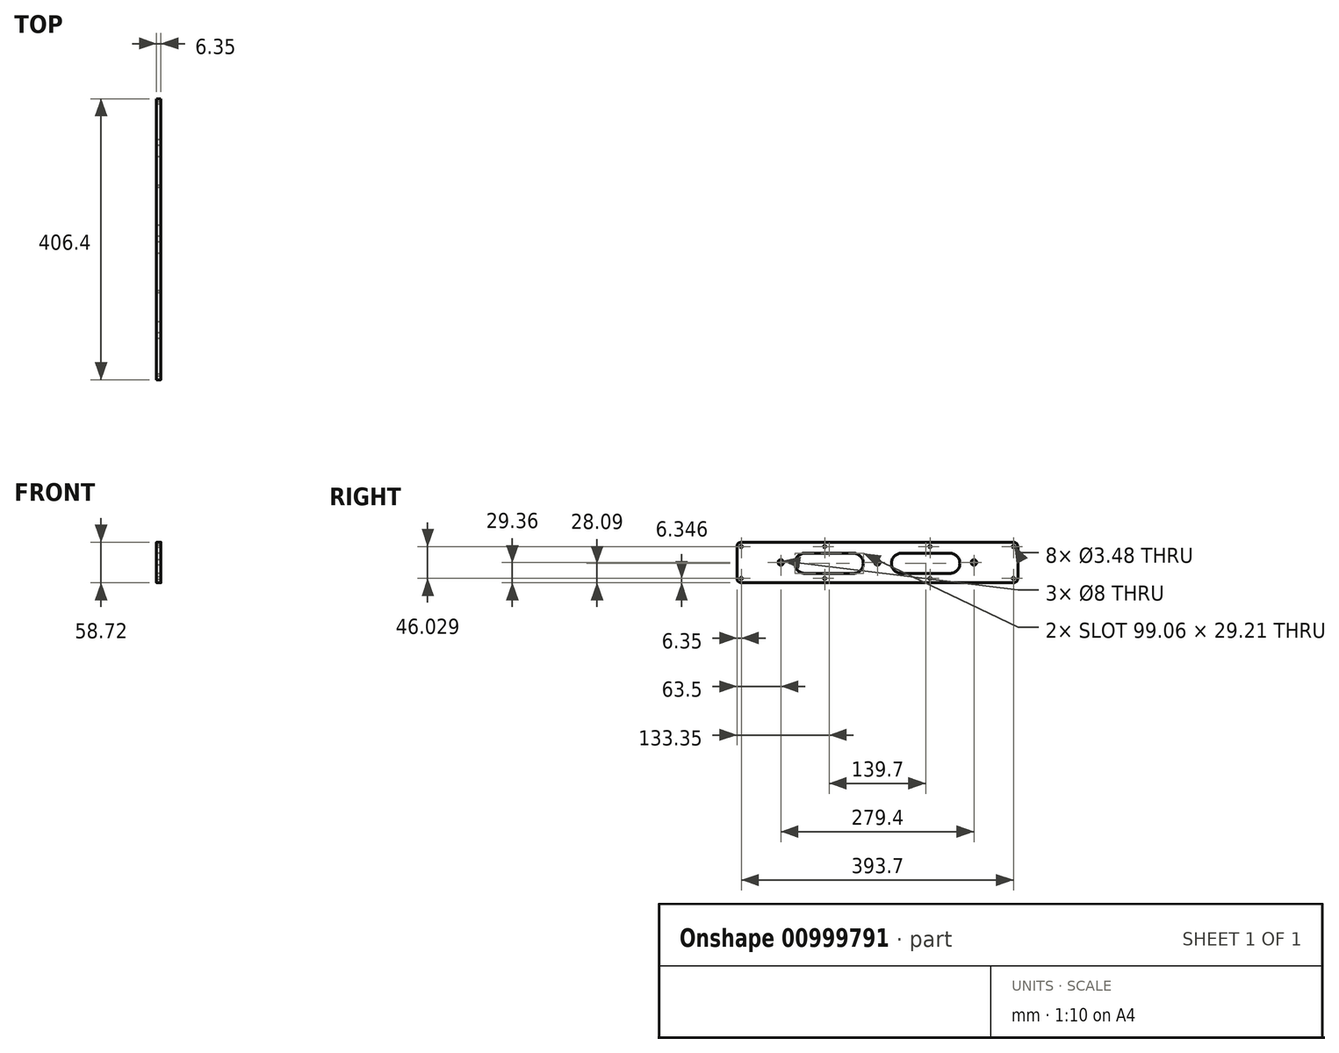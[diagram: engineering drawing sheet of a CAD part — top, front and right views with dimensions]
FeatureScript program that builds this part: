
annotation { "Feature Type Name" : "Feature", "Feature Type Description" : "" }
export const myFeature = defineFeature(function(context is Context, id is Id, definition is map)
    precondition{}
    {
        {
            var Q0;
            Q0=qCreatedBy(makeId("Right.planeOp"),FACE);
            var sketch = newSketch(context, id + "F0", { "sketchPlane" : qUnion([Q0])});
            skLineSegment(sketch, "E0.bottom", {"start": v(-196.85, -29.36) * mm, "end": v(196.85, -29.36) * mm});
            skLineSegment(sketch, "E0.top", {"start": v(-196.85, 29.36) * mm, "end": v(196.85, 29.36) * mm});
            skLineSegment(sketch, "E0.left", {"start": v(-203.2, -23.01) * mm, "end": v(-203.2, 23.01) * mm});
            skLineSegment(sketch, "E0.right", {"start": v(203.2, -23.01) * mm, "end": v(203.2, 23.01) * mm});
            skPoint(sketch, "E0.middle", {"position": v(0, 0) * mm});
            skCircle(sketch, "E1", {"center": v(0, 0) * mm, "radius": 4 * mm});
            skPoint(sketch, "E2.visualSharp", {"position": v(-203.2, 29.36) * mm});
            skArc(sketch, "E2.filletArc", {"start": v(-196.85, 29.36) * mm, "mid": v(-201.34, 27.5) * mm, "end": v(-203.2, 23.01) * mm});
            skPoint(sketch, "E3.visualSharp", {"position": v(-203.2, -29.36) * mm});
            skArc(sketch, "E3.filletArc", {"start": v(-203.2, -23.01) * mm, "mid": v(-201.34, -27.5) * mm, "end": v(-196.85, -29.36) * mm});
            skPoint(sketch, "E4.visualSharp", {"position": v(203.2, 29.36) * mm});
            skArc(sketch, "E4.filletArc", {"start": v(203.2, 23.01) * mm, "mid": v(201.34, 27.5) * mm, "end": v(196.85, 29.36) * mm});
            skPoint(sketch, "E5.visualSharp", {"position": v(203.2, -29.36) * mm});
            skArc(sketch, "E5.filletArc", {"start": v(196.85, -29.36) * mm, "mid": v(201.34, -27.5) * mm, "end": v(203.2, -23.01) * mm});
            skCircle(sketch, "E6", {"center": v(139.7, 0) * mm, "radius": 4 * mm});
            skCircle(sketch, "E7", {"center": v(-139.7, 0) * mm, "radius": 4 * mm});
            skCircle(sketch, "E8", {"center": v(196.85, 23.01) * mm, "radius": 1.74 * mm});
            skCircle(sketch, "E9", {"center": v(196.85, -23.01) * mm, "radius": 1.74 * mm});
            skCircle(sketch, "E10", {"center": v(-196.85, 23.01) * mm, "radius": 1.74 * mm});
            skCircle(sketch, "E11", {"center": v(-196.85, -23.01) * mm, "radius": 1.74 * mm});
            skCircle(sketch, "E12", {"center": v(-76.2, 23.01) * mm, "radius": 1.74 * mm});
            skCircle(sketch, "E13", {"center": v(76.2, 23.01) * mm, "radius": 1.74 * mm});
            skCircle(sketch, "E14", {"center": v(76.2, -23.01) * mm, "radius": 1.74 * mm});
            skCircle(sketch, "E15", {"center": v(-76.2, -23.01) * mm, "radius": 1.74 * mm});
            skArc(sketch, "E16", {"start": v(-104.78, -15.88) * mm, "mid": v(-119.38, -1.27) * mm, "end": v(-104.78, 13.33) * mm});
            skArc(sketch, "E17", {"start": v(-34.93, -15.87) * mm, "mid": v(-20.32, -1.27) * mm, "end": v(-34.93, 13.34) * mm});
            skLineSegment(sketch, "E18", {"start": v(-104.78, 13.33) * mm, "end": v(-34.93, 13.34) * mm});
            skLineSegment(sketch, "E19", {"start": v(-34.93, -15.88) * mm, "end": v(-104.78, -15.88) * mm});
            skArc(sketch, "E20", {"start": v(34.93, -15.87) * mm, "mid": v(20.32, -1.27) * mm, "end": v(34.93, 13.34) * mm});
            skArc(sketch, "E21", {"start": v(104.78, -15.87) * mm, "mid": v(119.38, -1.27) * mm, "end": v(104.78, 13.34) * mm});
            skLineSegment(sketch, "E22", {"start": v(34.93, 13.34) * mm, "end": v(104.78, 13.34) * mm});
            skLineSegment(sketch, "E23", {"start": v(34.93, -15.88) * mm, "end": v(104.78, -15.88) * mm});
            skLineSegment(sketch, "E24", {"start": v(-76.2, 23.01) * mm, "end": v(0, 23.01) * mm});
            skLineSegment(sketch, "E25", {"start": v(-76.2, -23.01) * mm, "end": v(0, -23.01) * mm});
            skLineSegment(sketch, "E26", {"start": v(-76.2, -23.01) * mm, "end": v(-76.2, -29.36) * mm});
            skLineSegment(sketch, "E27", {"start": v(-76.2, 23.01) * mm, "end": v(-76.2, 29.36) * mm});
            skSolve(sketch);
        }
        {
            var Q0;
            Q0=makeQuery(id+"F0.imprint","IMPRINT",FACE,{"disambiguationData":[TD([[makeQuery(id+"F0.imprint","IMPRINT",EDGE,{"derivedFrom":sQuery(id+"F0.wireOp",EDGE,"E0.bottom")}),1.0]])]});
            extrude(context, id + "F1", {"entities" : qUnion([Q0]), "depth" : 6.35 * mm, "offsetDistance" : 25.4 * mm});
        }
    });
